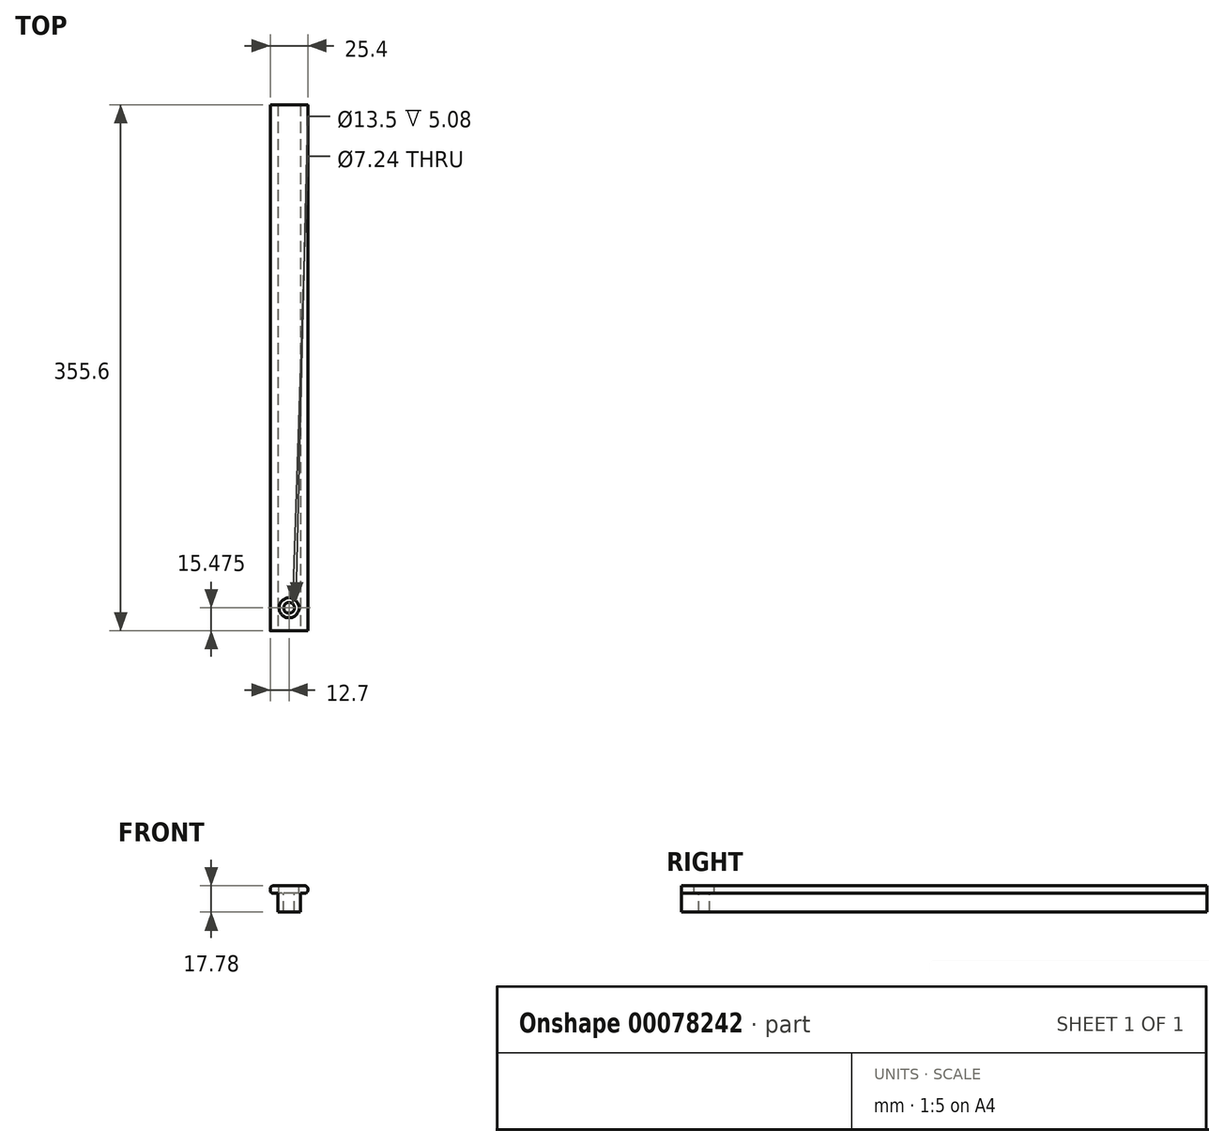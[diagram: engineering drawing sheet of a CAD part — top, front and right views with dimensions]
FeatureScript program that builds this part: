
annotation { "Feature Type Name" : "Feature", "Feature Type Description" : "" }
export const myFeature = defineFeature(function(context is Context, id is Id, definition is map)
    precondition{}
    {
        {
            var Q0;
            Q0=qCreatedBy(makeId("Front.planeOp"),FACE);
            var sketch = newSketch(context, id + "F0", { "sketchPlane" : qUnion([Q0])});
            skLineSegment(sketch, "E0", {"start": v(0, 17.78) * mm, "end": v(10.67, 17.78) * mm});
            skLineSegment(sketch, "E1", {"start": v(12.7, 15.75) * mm, "end": v(12.7, 14.73) * mm});
            skLineSegment(sketch, "E2", {"start": v(10.67, 12.7) * mm, "end": v(7.62, 12.7) * mm});
            skLineSegment(sketch, "E3", {"start": v(7.62, 12.7) * mm, "end": v(7.62, 0) * mm});
            skLineSegment(sketch, "E4", {"start": v(7.62, 0) * mm, "end": v(0, 0) * mm});
            skPoint(sketch, "E5.visualSharp", {"position": v(12.7, 17.78) * mm});
            skArc(sketch, "E5.filletArc", {"start": v(12.7, 15.75) * mm, "mid": v(12.1, 17.18) * mm, "end": v(10.67, 17.78) * mm});
            skPoint(sketch, "E6.visualSharp", {"position": v(12.7, 12.7) * mm});
            skArc(sketch, "E6.filletArc", {"start": v(10.67, 12.7) * mm, "mid": v(12.1, 13.3) * mm, "end": v(12.7, 14.73) * mm});
            skLineSegment(sketch, "E7.MirrorCS", {"start": v(0, 17.78) * mm, "end": v(-10.67, 17.78) * mm});
            skArc(sketch, "E8.MirrorCS", {"start": v(-12.7, 15.75) * mm, "mid": v(-12.1, 17.18) * mm, "end": v(-10.67, 17.78) * mm});
            skArc(sketch, "E9.MirrorCS", {"start": v(-10.67, 12.7) * mm, "mid": v(-12.1, 13.3) * mm, "end": v(-12.7, 14.73) * mm});
            skLineSegment(sketch, "E10.MirrorCS", {"start": v(-10.67, 12.7) * mm, "end": v(-7.62, 12.7) * mm});
            skLineSegment(sketch, "E11.MirrorCS", {"start": v(-7.62, 12.7) * mm, "end": v(-7.62, 0) * mm});
            skLineSegment(sketch, "E12.MirrorCS", {"start": v(-7.62, 0) * mm, "end": v(0, 0) * mm});
            skLineSegment(sketch, "E13.MirrorCS", {"start": v(-12.7, 15.75) * mm, "end": v(-12.7, 14.73) * mm});
            skSolve(sketch);
        }
        {
            var Q0;
            Q0=makeQuery(id+"F0.imprint","IMPRINT",FACE,{"disambiguationData":[TD([[makeQuery(id+"F0.imprint","IMPRINT",EDGE,{"derivedFrom":sQuery(id+"F0.wireOp",EDGE,"E0")}),-1.0]])]});
            extrude(context, id + "F1", {"entities" : qUnion([Q0]), "oppositeDirection" : true, "depth" : 355.6 * mm});
        }
        {
            var Q0;
            Q0=makeQuery(id+"F1.opExtrude","SWEPT_FACE",FACE,{"disambiguationData":[OSD([sQuery(id+"F0.wireOp",EDGE,"E0"),sQuery(id+"F0.wireOp",EDGE,"E7.MirrorCS")])]});
            var sketch = newSketch(context, id + "F2", { "sketchPlane" : qUnion([Q0])});
            skCircle(sketch, "E14", {"center": v(0, 15.47) * mm, "radius": 6.75 * mm});
            skCircle(sketch, "E15", {"center": v(0, 15.47) * mm, "radius": 4.05 * mm});
            skSolve(sketch);
        }
        {
            var Q0;
            Q0=makeQuery(id+"F2.imprint","IMPRINT",FACE,{"disambiguationData":[TD([[makeQuery(id+"F2.imprint","IMPRINT",EDGE,{"derivedFrom":sQuery(id+"F2.wireOp",EDGE,"E14")}),1.0]])]});
            var Q1;
            Q1=makeQuery(id+"F2.imprint","IMPRINT",FACE,{"disambiguationData":[TD([[makeQuery(id+"F2.imprint","IMPRINT",EDGE,{"derivedFrom":sQuery(id+"F2.wireOp",EDGE,"E15")}),1.0]])]});
            var Q2;
            Q2=sQuery(id+"F2.wireOp",EDGE,"E15");
            extrude(context, id + "F3", {"entities" : qUnion([Q0, Q1]), "operationType" : NewBodyOperationType.REMOVE, "surfaceEntities" : qUnion([Q2]), "oppositeDirection" : true, "depth" : 5.08 * mm});
        }
        {
            var Q0;
            Q0=makeQuery(id+"F1.opExtrude","SWEPT_FACE",FACE,{"disambiguationData":[OSD([sQuery(id+"F0.wireOp",EDGE,"E0"),sQuery(id+"F0.wireOp",EDGE,"E7.MirrorCS")])]});
            var sketch = newSketch(context, id + "F4", { "sketchPlane" : qUnion([Q0])});
            skCircle(sketch, "E16", {"center": v(0, 15.47) * mm, "radius": 3.62 * mm});
            skSolve(sketch);
        }
        {
            var Q0;
            Q0=makeQuery(id+"F4.imprint","IMPRINT",FACE,{"disambiguationData":[TD([[makeQuery(id+"F4.imprint","IMPRINT",EDGE,{"derivedFrom":sQuery(id+"F4.wireOp",EDGE,"E16")}),1.0]])]});
            extrude(context, id + "F5", {"entities" : qUnion([Q0]), "operationType" : NewBodyOperationType.REMOVE, "oppositeDirection" : true, "depth" : 25.4 * mm});
        }
    });
